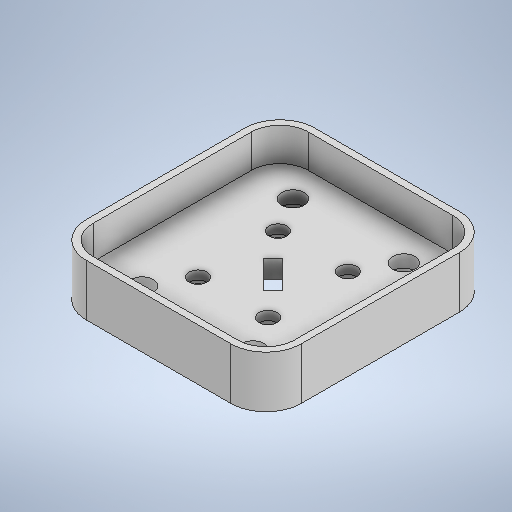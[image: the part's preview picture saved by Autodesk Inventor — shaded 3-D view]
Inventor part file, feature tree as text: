
AUTODESK INVENTOR PART (.ipt)
format: ipt  version: 2025 (Build 290162000, 162)  size: 358,400 bytes
history: native  units: mm
features: extrude x5, sketch x5, shell x1, thicken_offset x1, fillet x1, mirror x1
ambient origin geometry x8: Origin, YZ Plane, XZ Plane, XY Plane, X Axis, Y Axis, Z Axis, Center Point
bodies: Solid1 (feature_tree)
feature tree (14):
  extrude  "Extrusion1"  Depth=51.6mm
  shell  "Shell1"  Thickness=8.0mm
  thicken_offset  "Thicken1"
  extrude  "Extrusion2"  Depth=1.5mm
  extrude  "Extrusion3"  Depth=9.0mm
  extrude  "Extrusion4"  Depth=3.0mm
  extrude  "Extrusion5"  Depth=3.0mm
  fillet  "Fillet1"  [1 undecoded]
  mirror  "Mirror1"
  sketch  "Sketch1"  dims[d1=48.5mm d2=51.6mm d3=8.0mm]
  sketch  "Sketch2"  dims[d4=9.0mm d5=0.0mm d6=1.5mm]
  sketch  "Sketch3"  dims[d7=2.65mm d8=2.0mm d12=9.0mm]
  sketch  "Sketch4"  dims[d13=135.0deg d14=3.0mm]
  sketch  "Sketch5"  dims[d15=22.75mm d16=24.3mm d17=0.0mm d18=0.0mm d19=7.9mm d20=2.1mm d21=18.0mm d22=5.0mm d23=25.0mm d24=34.0mm d25=17.0mm d26=12.5mm d27=2.8mm d28=0.0mm d29=4.0mm d30=2.0mm d31=0.0mm d32=2.15mm d33=0.0mm d34=7.65mm d35=28.0mm d37=9.0mm d38=5.0mm d39=5.0mm d40=2.1mm d41=3.0mm]
note: 1 required parameter value undecoded (feature->parameter linkage not recoverable at this tier; creation-order binding heuristic only, values carry confidence <= 0.55)
